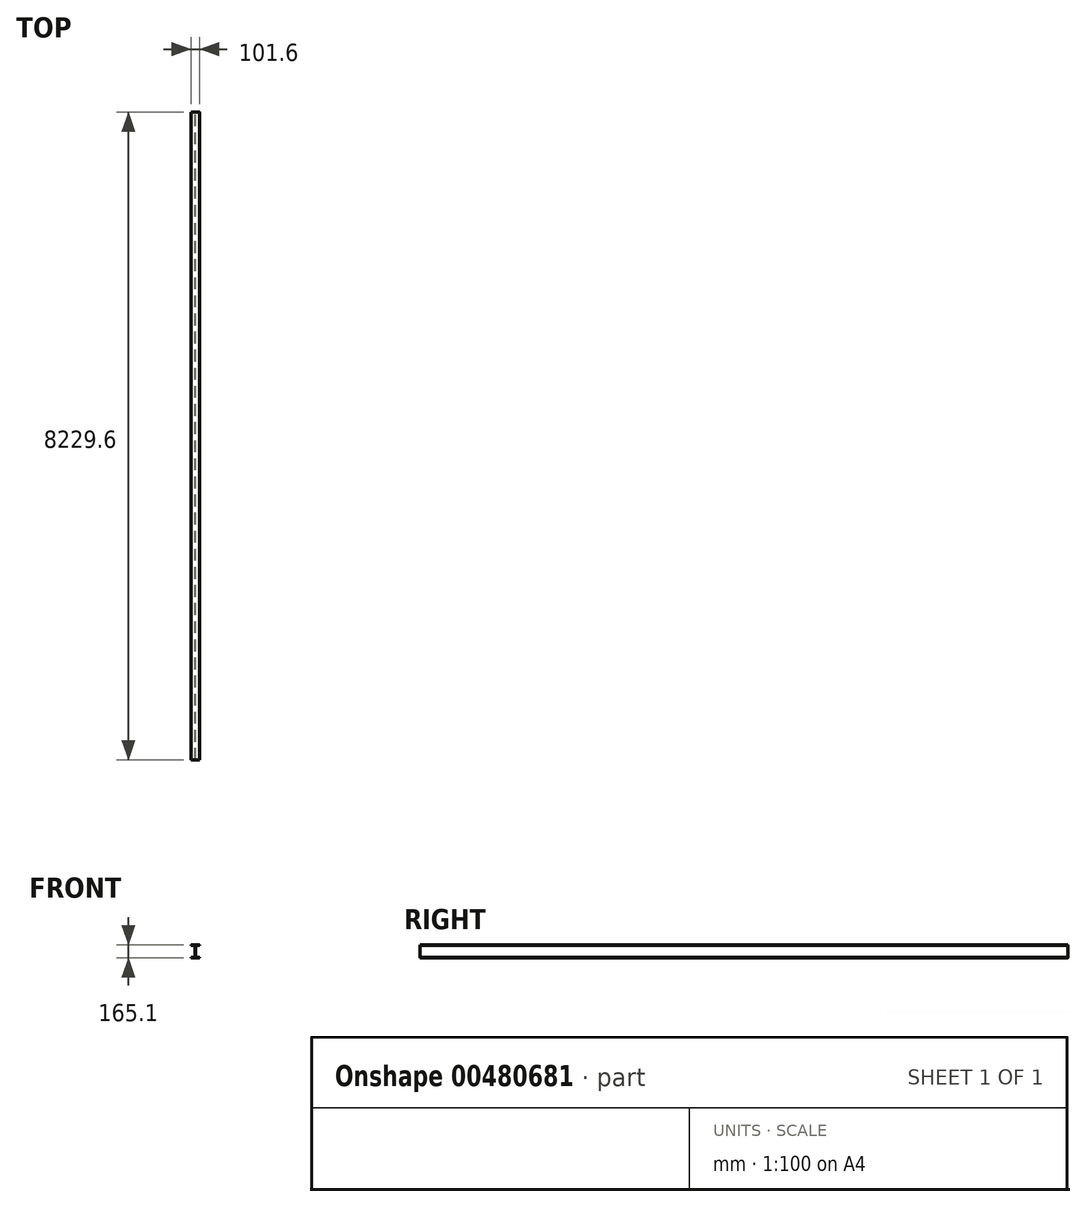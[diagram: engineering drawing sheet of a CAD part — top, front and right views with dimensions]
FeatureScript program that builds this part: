
annotation { "Feature Type Name" : "Feature", "Feature Type Description" : "" }
export const myFeature = defineFeature(function(context is Context, id is Id, definition is map)
    precondition{}
    {
        {
            var Q0;
            Q0=qCreatedBy(makeId("Front.planeOp"),FACE);
            var sketch = newSketch(context, id + "F0", { "sketchPlane" : qUnion([Q0])});
            skLineSegment(sketch, "E0", {"start": v(0, 137.16) * mm, "end": v(0, -15.24) * mm, "construction": true});
            skLineSegment(sketch, "E1", {"start": v(-50.55, 137.16) * mm, "end": v(-9.53, 137.16) * mm});
            skLineSegment(sketch, "E2", {"start": v(-50.55, -15.24) * mm, "end": v(-9.52, -15.24) * mm});
            skLineSegment(sketch, "E3.0", {"start": v(-50.55, -21.59) * mm, "end": v(50.55, -21.59) * mm});
            skLineSegment(sketch, "E4.0", {"start": v(-50.55, 143.5) * mm, "end": v(50.55, 143.5) * mm});
            skLineSegment(sketch, "E5.0", {"start": v(-3.17, 130.8) * mm, "end": v(-3.17, -8.89) * mm});
            skLineSegment(sketch, "E6.0", {"start": v(3.18, 130.8) * mm, "end": v(3.18, -8.89) * mm});
            skLineSegment(sketch, "E7", {"start": v(-50.8, -21.34) * mm, "end": v(-50.8, -15.5) * mm});
            skLineSegment(sketch, "E8", {"start": v(50.8, -15.5) * mm, "end": v(50.8, -21.34) * mm});
            skLineSegment(sketch, "E9", {"start": v(50.8, 137.41) * mm, "end": v(50.8, 143.26) * mm});
            skLineSegment(sketch, "E10", {"start": v(-50.8, 143.26) * mm, "end": v(-50.8, 137.41) * mm});
            skLineSegment(sketch, "E11.trimOffspring", {"start": v(9.53, 137.16) * mm, "end": v(50.55, 137.16) * mm});
            skLineSegment(sketch, "E12.trimOffspring", {"start": v(9.53, -15.24) * mm, "end": v(50.55, -15.24) * mm});
            skPoint(sketch, "E13.visualSharp", {"position": v(-3.18, 137.16) * mm});
            skArc(sketch, "E13.filletArc", {"start": v(-3.17, 130.8) * mm, "mid": v(-5.03, 135.3) * mm, "end": v(-9.53, 137.16) * mm});
            skPoint(sketch, "E14.visualSharp", {"position": v(3.18, 137.16) * mm});
            skArc(sketch, "E14.filletArc", {"start": v(9.53, 137.16) * mm, "mid": v(5.03, 135.3) * mm, "end": v(3.18, 130.8) * mm});
            skPoint(sketch, "E15.visualSharp", {"position": v(-3.17, -15.24) * mm});
            skArc(sketch, "E15.filletArc", {"start": v(-9.52, -15.24) * mm, "mid": v(-5.03, -13.38) * mm, "end": v(-3.17, -8.89) * mm});
            skPoint(sketch, "E16.visualSharp", {"position": v(3.18, -15.24) * mm});
            skArc(sketch, "E16.filletArc", {"start": v(3.18, -8.89) * mm, "mid": v(5.03, -13.38) * mm, "end": v(9.53, -15.24) * mm});
            skPoint(sketch, "E17.visualSharp", {"position": v(-50.8, -15.24) * mm});
            skArc(sketch, "E17.filletArc", {"start": v(-50.55, -15.24) * mm, "mid": v(-50.73, -15.31) * mm, "end": v(-50.8, -15.5) * mm});
            skPoint(sketch, "E18.visualSharp", {"position": v(-50.8, -21.59) * mm});
            skArc(sketch, "E18.filletArc", {"start": v(-50.8, -21.34) * mm, "mid": v(-50.73, -21.52) * mm, "end": v(-50.55, -21.59) * mm});
            skPoint(sketch, "E19.visualSharp", {"position": v(50.8, -21.59) * mm});
            skArc(sketch, "E19.filletArc", {"start": v(50.55, -21.59) * mm, "mid": v(50.73, -21.52) * mm, "end": v(50.8, -21.34) * mm});
            skPoint(sketch, "E20.visualSharp", {"position": v(50.8, -15.24) * mm});
            skArc(sketch, "E20.filletArc", {"start": v(50.8, -15.5) * mm, "mid": v(50.73, -15.31) * mm, "end": v(50.55, -15.24) * mm});
            skPoint(sketch, "E21.visualSharp", {"position": v(50.8, 137.16) * mm});
            skArc(sketch, "E21.filletArc", {"start": v(50.55, 137.16) * mm, "mid": v(50.73, 137.23) * mm, "end": v(50.8, 137.41) * mm});
            skPoint(sketch, "E22.visualSharp", {"position": v(50.8, 143.5) * mm});
            skArc(sketch, "E22.filletArc", {"start": v(50.8, 143.26) * mm, "mid": v(50.73, 143.44) * mm, "end": v(50.55, 143.5) * mm});
            skPoint(sketch, "E23.visualSharp", {"position": v(-50.8, 143.5) * mm});
            skArc(sketch, "E23.filletArc", {"start": v(-50.55, 143.5) * mm, "mid": v(-50.73, 143.44) * mm, "end": v(-50.8, 143.26) * mm});
            skPoint(sketch, "E24.visualSharp", {"position": v(-50.8, 137.16) * mm});
            skArc(sketch, "E24.filletArc", {"start": v(-50.8, 137.41) * mm, "mid": v(-50.73, 137.23) * mm, "end": v(-50.55, 137.16) * mm});
            skSolve(sketch);
        }
        {
            var Q0;
            Q0=makeQuery(id+"F0.imprint","IMPRINT",FACE,{"disambiguationData":[TD([[makeQuery(id+"F0.imprint","IMPRINT",EDGE,{"derivedFrom":sQuery(id+"F0.wireOp",EDGE,"E1")}),1.0]])]});
            extrude(context, id + "F1", {"entities" : qUnion([Q0]), "depth" : 8229.6 * mm});
        }
    });
